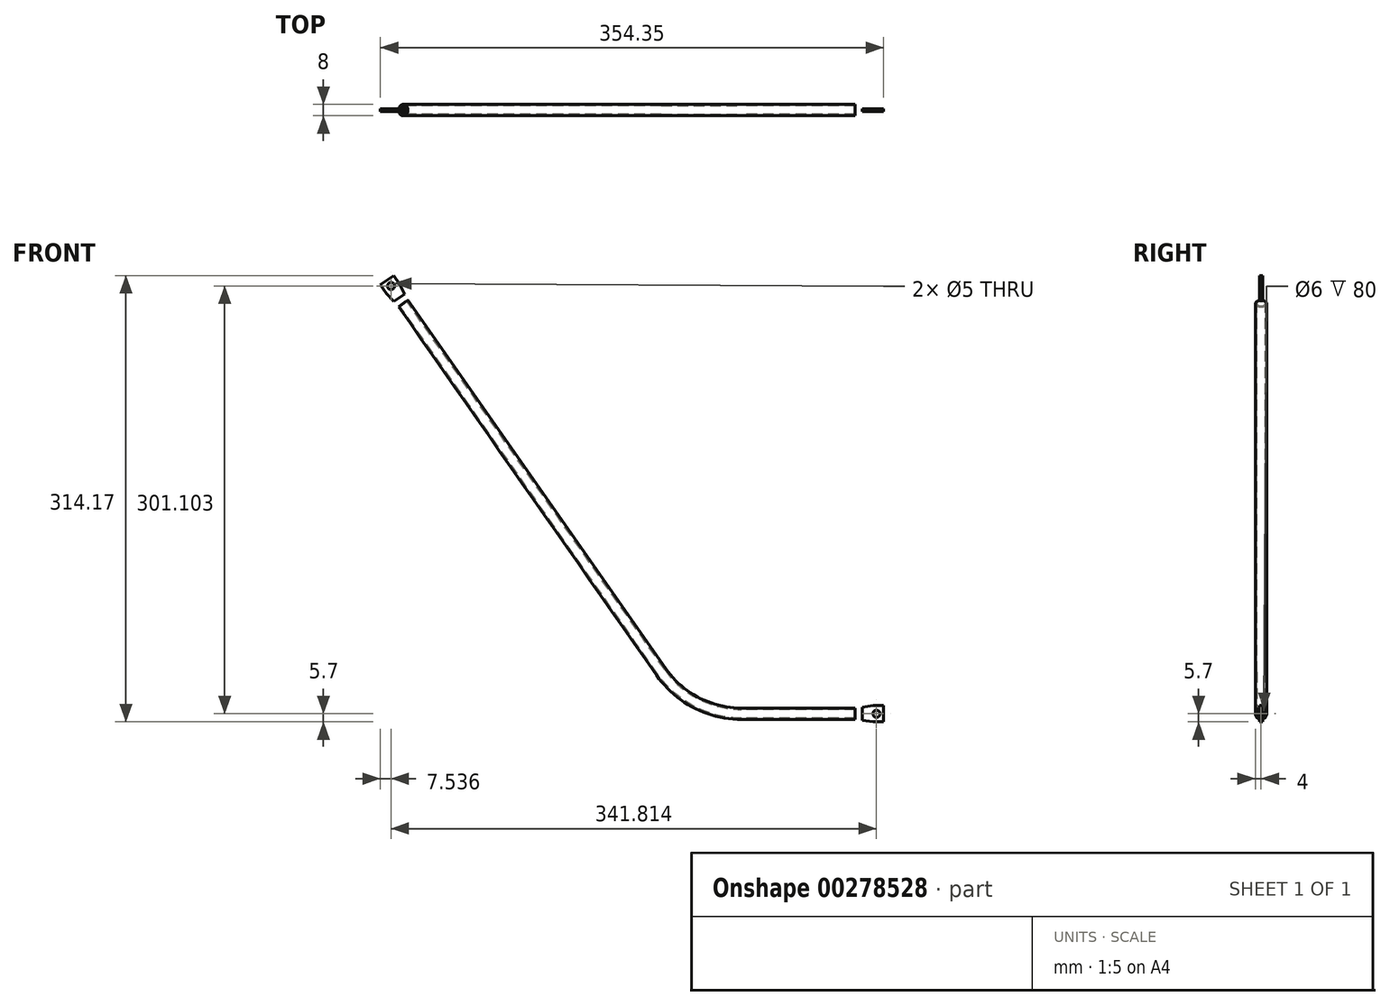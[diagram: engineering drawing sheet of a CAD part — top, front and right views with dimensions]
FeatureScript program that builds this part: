
annotation { "Feature Type Name" : "Feature", "Feature Type Description" : "" }
export const myFeature = defineFeature(function(context is Context, id is Id, definition is map)
    precondition{}
    {
        {
            var Q0;
            Q0=qCreatedBy(makeId("Front.planeOp"),FACE);
            var sketch = newSketch(context, id + "F0", { "sketchPlane" : qUnion([Q0])});
            skLineSegment(sketch, "E0", {"start": v(0, 0) * mm, "end": v(-100, 0) * mm});
            skLineSegment(sketch, "E1", {"start": v(-156.62, 29.47) * mm, "end": v(-349.68, 305.2) * mm});
            skArc(sketch, "E2", {"start": v(-156.62, 29.47) * mm, "mid": v(-131.91, 7.8) * mm, "end": v(-100, 0) * mm});
            skSolve(sketch);
        }
        {
            var Q0;
            Q0=qCreatedBy(makeId("Right.planeOp"),FACE);
            var sketch = newSketch(context, id + "F1", { "sketchPlane" : qUnion([Q0])});
            skCircle(sketch, "E3", {"center": v(0, 0) * mm, "radius": 4 * mm});
            skCircle(sketch, "E4", {"center": v(0, 0) * mm, "radius": 3 * mm});
            skSolve(sketch);
        }
        {
            var Q0;
            Q0 = qSketchRegion(id + "F1", true);
            var Q1;
            Q1 = qConstructionFilter(qBodyType(qCreatedBy(id + "F0" ,EDGE), BodyType.WIRE), ConstructionObject.NO);
            sweep(context, id + "F2", {"profiles" : qUnion([Q0]), "path" : qUnion([Q1])});
        }
        {
            var Q0;
            Q0=qCreatedBy(makeId("Front.planeOp"),FACE);
            var sketch = newSketch(context, id + "F3", { "sketchPlane" : qUnion([Q0])});
            skLineSegment(sketch, "E5.bottom", {"start": v(-20, 13.8) * mm, "end": v(20, 13.8) * mm});
            skLineSegment(sketch, "E5.top", {"start": v(-20, -13.8) * mm, "end": v(20, -13.8) * mm});
            skLineSegment(sketch, "E5.left", {"start": v(-20, 13.8) * mm, "end": v(-20, -13.8) * mm});
            skLineSegment(sketch, "E5.right", {"start": v(20, 13.8) * mm, "end": v(20, -13.8) * mm});
            skPoint(sketch, "E5.middle", {"position": v(0, 0) * mm});
            skLineSegment(sketch, "E6.0", {"start": v(-352.96, 302.9) * mm, "end": v(-346.4, 307.5) * mm});
            skPoint(sketch, "E7", {"position": v(-349.68, 305.2) * mm});
            skLineSegment(sketch, "E8", {"start": v(-346.4, 307.5) * mm, "end": v(-334.93, 291.11) * mm});
            skLineSegment(sketch, "E9", {"start": v(-352.96, 302.9) * mm, "end": v(-341.49, 286.52) * mm});
            skLineSegment(sketch, "E10", {"start": v(-341.49, 286.52) * mm, "end": v(-334.93, 291.11) * mm});
            skSolve(sketch);
        }
        {
            var Q0;
            Q0 = qSketchRegion(id + "F3", true);
            extrude(context, id + "F4", {"entities" : qUnion([Q0]), "operationType" : NewBodyOperationType.REMOVE, "endBound" : BoundingType.SYMMETRIC, "oppositeDirection" : true, "depth" : 25 * mm, "offsetDistance" : 25 * mm});
        }
        {
            var Q0;
            Q0=qCreatedBy(makeId("Front.planeOp"),FACE);
            var sketch = newSketch(context, id + "F5", { "sketchPlane" : qUnion([Q0])});
            skLineSegment(sketch, "E11", {"start": v(0, 5.7) * mm, "end": v(0, -5.7) * mm});
            skLineSegment(sketch, "E12", {"start": v(0, 5.7) * mm, "end": v(-7.5, 5.7) * mm});
            skLineSegment(sketch, "E13", {"start": v(0, -5.7) * mm, "end": v(-7.5, -5.7) * mm});
            skLineSegment(sketch, "E14", {"start": v(0, 0) * mm, "end": v(-19.87, 0) * mm, "construction": true});
            skLineSegment(sketch, "E15", {"start": v(-15, 4.5) * mm, "end": v(-15, -4.5) * mm});
            skPoint(sketch, "E16", {"position": v(-15, 0) * mm});
            skLineSegment(sketch, "E17", {"start": v(-15, 4.5) * mm, "end": v(-7.5, 5.7) * mm});
            skLineSegment(sketch, "E18", {"start": v(-7.5, -5.7) * mm, "end": v(-15, -4.5) * mm});
            skLineSegment(sketch, "E19.0", {"start": v(-341.49, 286.52) * mm, "end": v(-334.93, 291.11) * mm, "construction": true});
            skLineSegment(sketch, "E20", {"start": v(-338.2, 288.82) * mm, "end": v(-358.6, 317.93) * mm, "construction": true});
            skLineSegment(sketch, "E21", {"start": v(-354.35, 301.93) * mm, "end": v(-345.01, 308.47) * mm});
            skPoint(sketch, "E22", {"position": v(-349.68, 305.2) * mm});
            skLineSegment(sketch, "E23", {"start": v(-354.35, 301.93) * mm, "end": v(-350.05, 295.79) * mm});
            skLineSegment(sketch, "E24", {"start": v(-345.01, 308.47) * mm, "end": v(-340.71, 302.32) * mm});
            skLineSegment(sketch, "E25", {"start": v(-344.76, 290.33) * mm, "end": v(-337.4, 295.5) * mm});
            skPoint(sketch, "E26", {"position": v(-341.08, 292.91) * mm});
            skLineSegment(sketch, "E27", {"start": v(-350.05, 295.79) * mm, "end": v(-344.76, 290.33) * mm});
            skLineSegment(sketch, "E28", {"start": v(-340.71, 302.32) * mm, "end": v(-337.4, 295.5) * mm});
            skSolve(sketch);
        }
        {
            var Q0;
            Q0=makeQuery(id+"F5.imprint","IMPRINT",FACE,{"disambiguationData":[TD([[makeQuery(id+"F5.imprint","IMPRINT",EDGE,{"derivedFrom":sQuery(id+"F5.wireOp",EDGE,"E11")}),-1.0]])]});
            var Q1;
            Q1=makeQuery(id+"F5.imprint","IMPRINT",FACE,{"disambiguationData":[TD([[makeQuery(id+"F5.imprint","IMPRINT",EDGE,{"derivedFrom":sQuery(id+"F5.wireOp",EDGE,"E21")}),-1.0]])]});
            extrude(context, id + "F6", {"entities" : qUnion([Q0, Q1]), "endBound" : BoundingType.SYMMETRIC, "depth" : 2 * mm, "offsetDistance" : 25 * mm, "hasSecondDirection" : true, "secondDirectionOppositeDirection" : true, "secondDirectionDepth" : 25 * mm});
        }
        {
            var Q0;
            Q0=makeQuery(id+"F6.opExtrude","SWEPT_FACE",FACE,{"disambiguationData":[OSD([sQuery(id+"F5.wireOp",EDGE,"E25")])]});
            var Q1;
            Q1=makeQuery(id+"F4.boolean.opBoolean","COPY",FACE,{"derivedFrom":makeQuery(id+"F4.opExtrude","SWEPT_FACE",FACE,{"disambiguationData":[OSD([sQuery(id+"F3.wireOp",EDGE,"E10")])]})});
            var Q2;
            Q2=makeQuery(id+"F6.opExtrude","SWEPT_FACE",FACE,{"disambiguationData":[OSD([sQuery(id+"F5.wireOp",EDGE,"E25")])]});
            var Q3;
            Q3=makeQuery(id+"F4.boolean.opBoolean","INTERSECT",EDGE,{"derivedFrom":[makeQuery(id+"F2.opSweep","SWEPT_FACE",FACE,{"disambiguationData":[OSD([sQuery(id+"F0.wireOp",EDGE,"E1"),sQuery(id+"F1.wireOp",EDGE,"E3")])]}),makeQuery(id+"F4.opExtrude","SWEPT_FACE",FACE,{"disambiguationData":[OSD([sQuery(id+"F3.wireOp",EDGE,"E10")])]})]});
            loft(context, id + "F7", {"bodyType" : ToolBodyType.SURFACE, "operationType" : NewBodyOperationType.ADD, "sheetProfilesArray" : [{ "sheetProfileEntities" : qUnion([Q0]) }, { "sheetProfileEntities" : qUnion([Q1]) }], "wireProfilesArray" : [{ "wireProfileEntities" : qUnion([Q2]) }, { "wireProfileEntities" : qUnion([Q3]) }]});
        }
        {
            var Q0;
            Q0=makeQuery(id+"F6.opExtrude","SWEPT_FACE",FACE,{"disambiguationData":[OSD([sQuery(id+"F5.wireOp",EDGE,"E15")])]});
            var Q1;
            Q1=makeQuery(id+"F4.boolean.opBoolean","INTERSECT",EDGE,{"derivedFrom":[makeQuery(id+"F2.opSweep","SWEPT_FACE",FACE,{"disambiguationData":[OSD([sQuery(id+"F0.wireOp",EDGE,"E0"),sQuery(id+"F1.wireOp",EDGE,"E3")])]}),makeQuery(id+"F4.opExtrude","SWEPT_FACE",FACE,{"disambiguationData":[OSD([sQuery(id+"F3.wireOp",EDGE,"E5.left")])]})]});
            var Q2;
            Q2=makeQuery(id+"F6.opExtrude","SWEPT_FACE",FACE,{"disambiguationData":[OSD([sQuery(id+"F5.wireOp",EDGE,"E15")])]});
            loft(context, id + "F8", {"bodyType" : ToolBodyType.SURFACE, "sheetProfilesArray" : [{ "sheetProfileEntities" : qUnion([Q0]) }], "wireProfilesArray" : [{ "wireProfileEntities" : qUnion([Q1]) }, { "wireProfileEntities" : qUnion([Q2]) }]});
        }
        {
            var Q0;
            Q0=makeQuery(id+"F6.opExtrude","CAP_FACE",FACE,{"disambiguationData":[OSD([sQuery(id+"F5.wireOp",EDGE,"E21"),sQuery(id+"F5.wireOp",EDGE,"E23"),sQuery(id+"F5.wireOp",EDGE,"E24"),sQuery(id+"F5.wireOp",EDGE,"E25"),sQuery(id+"F5.wireOp",EDGE,"E27"),sQuery(id+"F5.wireOp",EDGE,"E28")])],"isStart":false});
            var sketch = newSketch(context, id + "F9", { "sketchPlane" : qUnion([Q0])});
            skLineSegment(sketch, "E29", {"start": v(-349.68, 305.2) * mm, "end": v(-341.08, 292.91) * mm, "construction": true});
            skCircle(sketch, "E30", {"center": v(-346.81, 301.1) * mm, "radius": 2.5 * mm});
            skLineSegment(sketch, "E31", {"start": v(0, 0) * mm, "end": v(-10, 0) * mm, "construction": true});
            skCircle(sketch, "E32", {"center": v(-5, 0) * mm, "radius": 2.5 * mm});
            skSolve(sketch);
        }
        {
            var Q0;
            Q0 = qSketchRegion(id + "F9", true);
            extrude(context, id + "F10", {"entities" : qUnion([Q0]), "operationType" : NewBodyOperationType.REMOVE, "endBound" : BoundingType.THROUGH_ALL, "oppositeDirection" : true, "depth" : 25 * mm, "offsetDistance" : 25 * mm});
        }
    });
